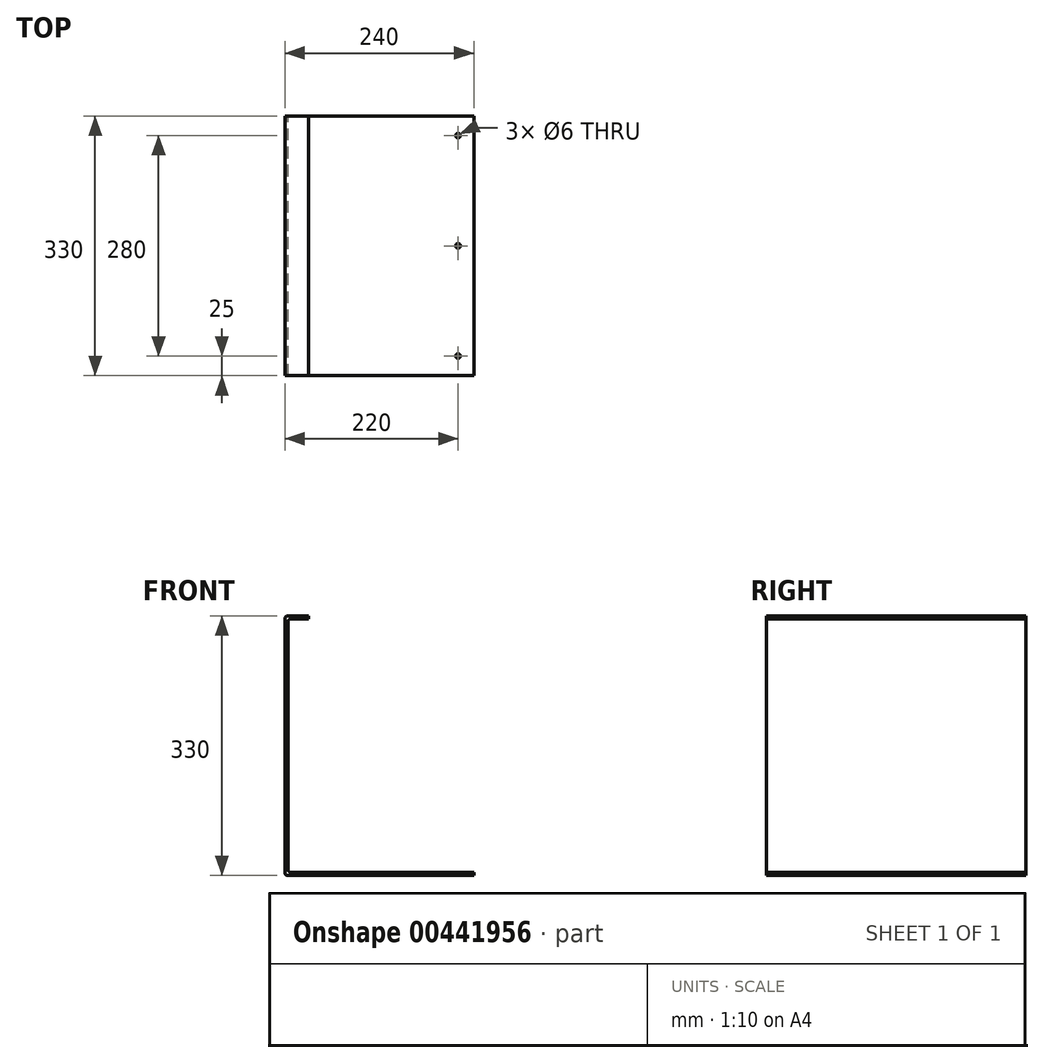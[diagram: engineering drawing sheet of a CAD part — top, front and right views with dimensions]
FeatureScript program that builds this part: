
annotation { "Feature Type Name" : "Feature", "Feature Type Description" : "" }
export const myFeature = defineFeature(function(context is Context, id is Id, definition is map)
    precondition{}
    {
        {
            var Q0;
            Q0=qCreatedBy(makeId("Front.planeOp"),FACE);
            var sketch = newSketch(context, id + "F0", { "sketchPlane" : qUnion([Q0])});
            skLineSegment(sketch, "E0", {"start": v(0, 4) * mm, "end": v(0, 326) * mm});
            skLineSegment(sketch, "E1", {"start": v(4, 330) * mm, "end": v(30, 330) * mm});
            skLineSegment(sketch, "E2", {"start": v(30, 330) * mm, "end": v(30, 326) * mm});
            skLineSegment(sketch, "E3", {"start": v(30, 326) * mm, "end": v(8, 326) * mm});
            skLineSegment(sketch, "E4", {"start": v(4, 322) * mm, "end": v(4, 8) * mm});
            skLineSegment(sketch, "E5", {"start": v(8, 4) * mm, "end": v(240, 4) * mm});
            skLineSegment(sketch, "E6", {"start": v(240, 4) * mm, "end": v(240, 0) * mm});
            skLineSegment(sketch, "E7", {"start": v(240, 0) * mm, "end": v(4, 0) * mm});
            skPoint(sketch, "E8.visualSharp", {"position": v(0, 0) * mm});
            skArc(sketch, "E8.filletArc", {"start": v(0, 4) * mm, "mid": v(1.17, 1.17) * mm, "end": v(4, 0) * mm});
            skArc(sketch, "E9.filletArc", {"start": v(4, 8) * mm, "mid": v(5.17, 5.17) * mm, "end": v(8, 4) * mm});
            skPoint(sketch, "E10.visualSharp", {"position": v(0, 330) * mm});
            skArc(sketch, "E10.filletArc", {"start": v(4, 330) * mm, "mid": v(1.17, 328.83) * mm, "end": v(0, 326) * mm});
            skArc(sketch, "E11.filletArc", {"start": v(8, 326) * mm, "mid": v(5.17, 324.83) * mm, "end": v(4, 322) * mm});
            skSolve(sketch);
        }
        {
            var Q0;
            Q0 = qSketchRegion(id + "F0", true);
            extrude(context, id + "F1", {"entities" : qUnion([Q0]), "endBound" : BoundingType.SYMMETRIC, "depth" : 330 * mm});
        }
        {
            var Q0;
            Q0=makeQuery(id+"F1.opExtrude","SWEPT_FACE",FACE,{"disambiguationData":[OSD([sQuery(id+"F0.wireOp",EDGE,"E5")])]});
            var sketch = newSketch(context, id + "F2", { "sketchPlane" : qUnion([Q0])});
            skCircle(sketch, "E12", {"center": v(220, 0) * mm, "radius": 3 * mm});
            skPoint(sketch, "E12.centerSnap0", {"position": v(240, 0) * mm});
            skCircle(sketch, "E13", {"center": v(220, 140) * mm, "radius": 3 * mm});
            skCircle(sketch, "E14", {"center": v(220, -140) * mm, "radius": 3 * mm});
            skSolve(sketch);
        }
        {
            var Q0;
            Q0=makeQuery(id+"F2.imprint","IMPRINT",FACE,{"disambiguationData":[TD([[makeQuery(id+"F2.imprint","IMPRINT",EDGE,{"derivedFrom":sQuery(id+"F2.wireOp",EDGE,"E13")}),1.0]])]});
            var Q1;
            Q1=makeQuery(id+"F2.imprint","IMPRINT",FACE,{"disambiguationData":[TD([[makeQuery(id+"F2.imprint","IMPRINT",EDGE,{"derivedFrom":sQuery(id+"F2.wireOp",EDGE,"E12")}),1.0]])]});
            var Q2;
            Q2=makeQuery(id+"F2.imprint","IMPRINT",FACE,{"disambiguationData":[TD([[makeQuery(id+"F2.imprint","IMPRINT",EDGE,{"derivedFrom":sQuery(id+"F2.wireOp",EDGE,"E14")}),1.0]])]});
            var Q3;
            Q3=sQuery(id+"F2.wireOp",EDGE,"E13");
            var Q4;
            Q4=sQuery(id+"F2.wireOp",EDGE,"E12");
            var Q5;
            Q5=sQuery(id+"F2.wireOp",EDGE,"E14");
            extrude(context, id + "F3", {"entities" : qUnion([Q0, Q1, Q2]), "operationType" : NewBodyOperationType.REMOVE, "surfaceEntities" : qUnion([Q3, Q4, Q5]), "endBound" : BoundingType.THROUGH_ALL, "depth" : 202 * mm, "hasSecondDirection" : true, "secondDirectionOppositeDirection" : true, "secondDirectionDepth" : 25 * mm});
        }
    });
